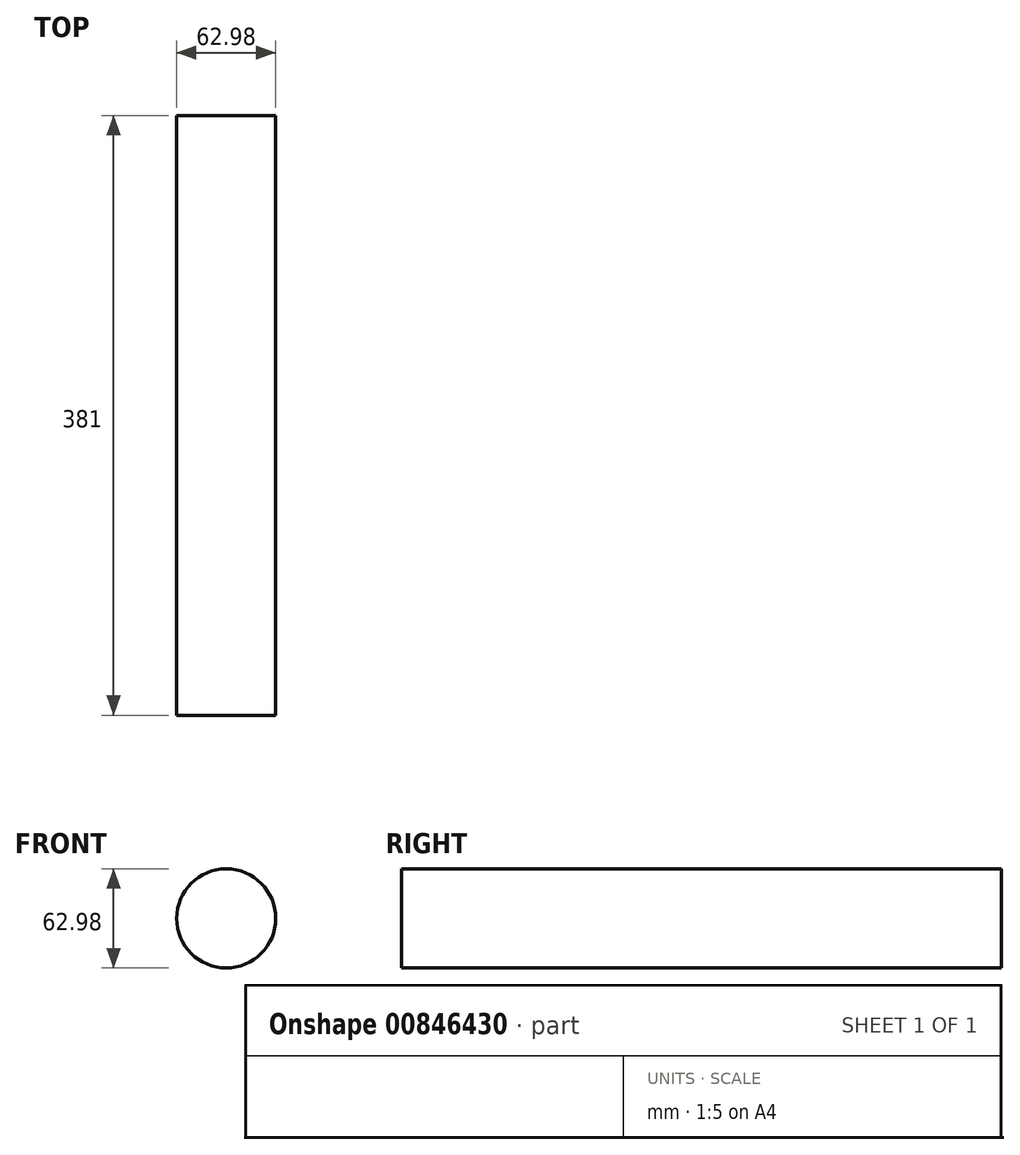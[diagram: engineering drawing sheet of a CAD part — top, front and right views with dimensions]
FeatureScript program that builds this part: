
annotation { "Feature Type Name" : "Feature", "Feature Type Description" : "" }
export const myFeature = defineFeature(function(context is Context, id is Id, definition is map)
    precondition{}
    {
        {
            var Q0;
            Q0=qCreatedBy(makeId("Front.planeOp"),FACE);
            var sketch = newSketch(context, id + "F0", { "sketchPlane" : qUnion([Q0])});
            skCircle(sketch, "E0", {"center": v(0, 0) * mm, "radius": 31.5 * mm});
            skSolve(sketch);
        }
        {
            var Q0;
            Q0=qSketchRegion(id+"F0",true);
            extrude(context, id + "F1", {"entities" : qUnion([Q0]), "depth" : 381 * mm, "offsetDistance" : 25.4 * mm});
        }
    });
